# Revit family: Gira_0211135
name_source: partatom
category: Electrical Fixtures
revit_build: Autodesk Revit 2017 (Build: 20160225_1515(x64)
units: mm (PartAtom-declared; Revit-internal decimal feet)

## family parameters
Cut with Voids When Loaded = No
Host = Face
Maintain Annotation Orientation = No
Part Type = Normal
Room Calculation Point = No
Round Connector Dimension = Use Diameter
Shared = No

## types (1)
- Cov.fr. 1-g Gira Studio black gl.
    Available = No
    BIM (1) = https://media.stage.bim.site
    BIM (2) = https://media.stage.bim.site
    Category = Cover frame for domestic switching devices
    Data sheet (1) = https://katalog.gira.de
    Default Elevation = 1219 mm
    Description = Cov.fr.1g Stud. GBk,Gira Studio cover frame,black glass,1-gang,Installation in standard device boxes, can be extended as required through installation in device boxes with spacer glands.,For surface-mounted installation: Gira Studio, housing, 1-gang, with cover frame, 1-gang, can be extended as required.
    GTIN = 4010337045656
    HAN = 0211135
    HeinzeBIM = https://bimportal.heinze.de
    Label space/information surface = No
    Manufacturer = Gira
    Manufacturer URL = https://www.gira.de
    Name = Cov.fr. 1-g Gira Studio black gl.
    Transparent = No
    URL = http://katalog.gira.de

## geometry (parser evidence)
native form markers: Blend x2, Sweep x3
no freeform markers — native parametric forms only
